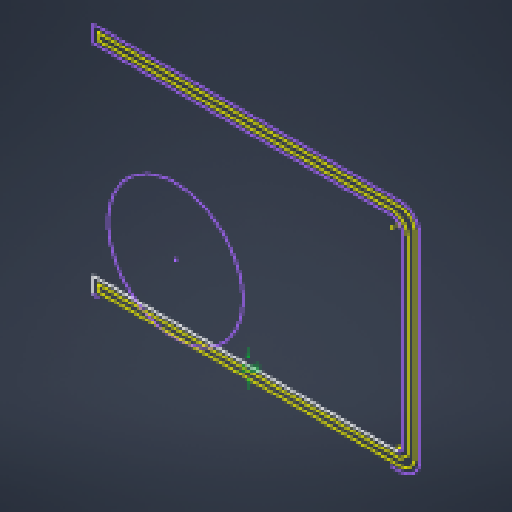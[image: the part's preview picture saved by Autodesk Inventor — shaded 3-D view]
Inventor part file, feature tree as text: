
AUTODESK INVENTOR PART (.ipt)
format: ipt  version: 2024 (Build 280153000, 153)  size: 111,104 bytes
history: native  units: in
note: dims shown in document units (in); Inventor stores cm internally (conversion verified against a paired STEP export)
features: other x3, sketch x1, reference x1
ambient origin geometry x8: Origin, YZ Plane, XZ Plane, XY Plane, X Axis, Y Axis, Z Axis, Center Point
feature tree (5):
  sketch  "Sketch1"  dims[d0=0.1181in]
  reference  "Reference1"
  other  "<userpath>\Desktop\Camera_Mount.iam"
  other  "Camera_Mount.iam"
  other  "Head_Box_Base:1"
